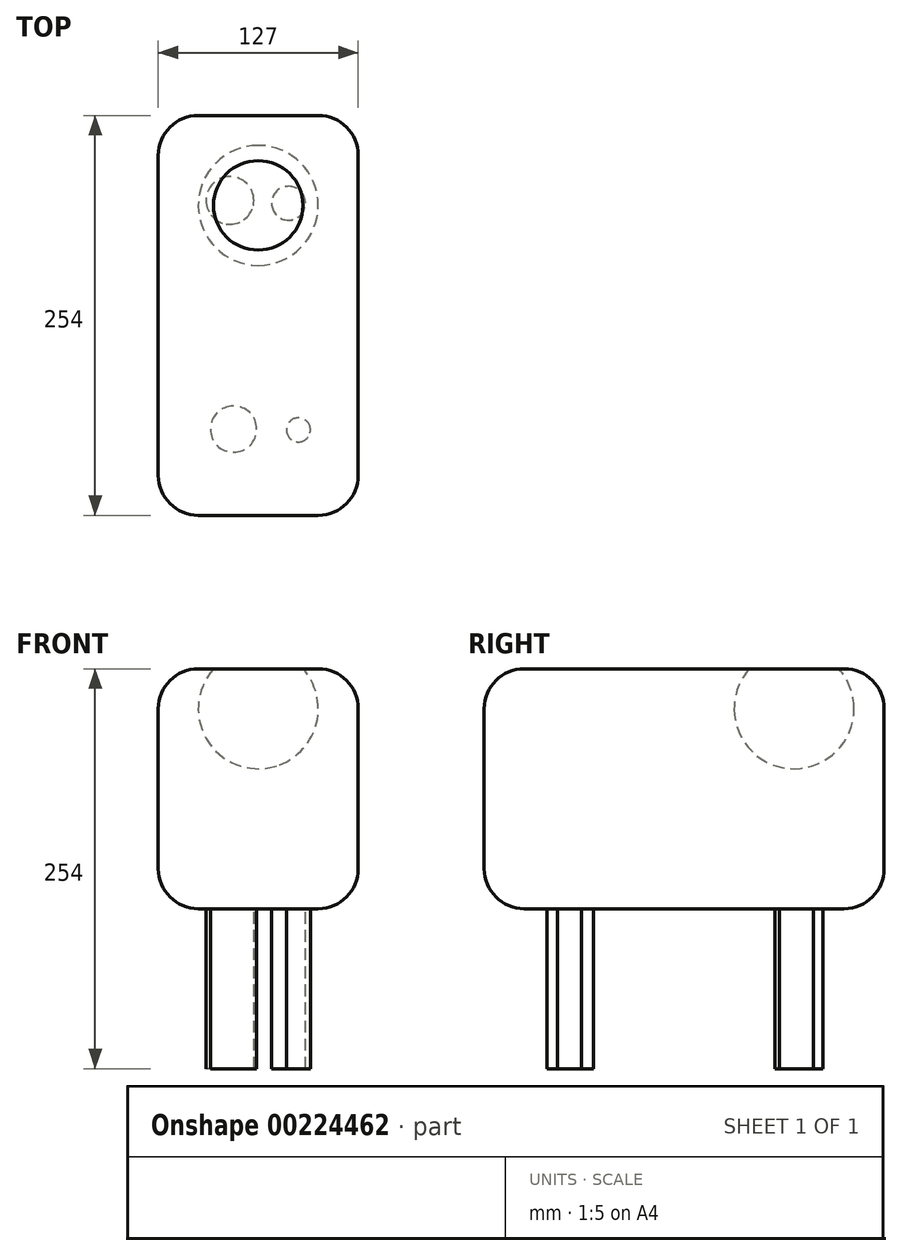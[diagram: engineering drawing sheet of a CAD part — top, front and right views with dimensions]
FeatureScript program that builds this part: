
annotation { "Feature Type Name" : "Feature", "Feature Type Description" : "" }
export const myFeature = defineFeature(function(context is Context, id is Id, definition is map)
    precondition{}
    {
        {
            var Q0;
            Q0=qCreatedBy(makeId("Right.planeOp"),FACE);
            var sketch = newSketch(context, id + "F0", { "sketchPlane" : qUnion([Q0])});
            skLineSegment(sketch, "E0.bottom", {"start": v(0, 0) * mm, "end": v(254, 0) * mm});
            skLineSegment(sketch, "E0.top", {"start": v(0, 152.4) * mm, "end": v(254, 152.4) * mm});
            skLineSegment(sketch, "E0.left", {"start": v(0, 0) * mm, "end": v(0, 152.4) * mm});
            skLineSegment(sketch, "E0.right", {"start": v(254, 0) * mm, "end": v(254, 152.4) * mm});
            skSolve(sketch);
        }
        {
            var Q0;
            Q0 = qSketchRegion(id + "F0", true);
            extrude(context, id + "F1", {"entities" : qUnion([Q0]), "depth" : 127 * mm});
        }
        {
            var Q0;
            Q0=makeQuery(id+"F1.opExtrude","SWEPT_FACE",FACE,{"disambiguationData":[OSD([sQuery(id+"F0.wireOp",EDGE,"E0.top")])]});
            var Q1;
            Q1=makeQuery(id+"F1.opExtrude","SWEPT_FACE",FACE,{"disambiguationData":[OSD([sQuery(id+"F0.wireOp",EDGE,"E0.right")])]});
            var Q2;
            Q2=makeQuery(id+"F1.opExtrude","CAP_FACE",FACE,{"disambiguationData":[OSD([sQuery(id+"F0.wireOp",EDGE,"E0.bottom"),sQuery(id+"F0.wireOp",EDGE,"E0.top"),sQuery(id+"F0.wireOp",EDGE,"E0.left"),sQuery(id+"F0.wireOp",EDGE,"E0.right")])],"isStart":false});
            var Q3;
            Q3=makeQuery(id+"F1.opExtrude","CAP_FACE",FACE,{"disambiguationData":[OSD([sQuery(id+"F0.wireOp",EDGE,"E0.bottom"),sQuery(id+"F0.wireOp",EDGE,"E0.top"),sQuery(id+"F0.wireOp",EDGE,"E0.left"),sQuery(id+"F0.wireOp",EDGE,"E0.right")])],"isStart":true});
            var Q4;
            Q4=makeQuery(id+"F1.opExtrude","SWEPT_FACE",FACE,{"disambiguationData":[OSD([sQuery(id+"F0.wireOp",EDGE,"E0.bottom")])]});
            fillet(context, id + "F2", {"entities" : qUnion([Q0, Q1, Q2, Q3, Q4]), "radius" : 25.4 * mm, "tangentPropagation" : true, "allowEdgeOverflow" : false});
        }
        {
            var Q0;
            Q0=makeQuery(id+"F1.opExtrude","SWEPT_FACE",FACE,{"disambiguationData":[OSD([sQuery(id+"F0.wireOp",EDGE,"E0.top")])]});
            cPlane(context, id + "F3", {"entities" : qUnion([Q0]), "cplaneType" : CPlaneType.OFFSET, "offset" : 25.4 * mm, "oppositeDirection" : true, "width" : 152.4 * mm, "height" : 152.4 * mm});
        }
        {
            var Q0;
            Q0=qCreatedBy(id+"F3.planeOp",FACE);
            var sketch = newSketch(context, id + "F4", { "sketchPlane" : qUnion([Q0])});
            skArc(sketch, "E1", {"start": v(63.5, 234.95) * mm, "mid": v(25.4, 196.85) * mm, "end": v(63.5, 158.75) * mm});
            skLineSegment(sketch, "E2", {"start": v(63.5, 234.95) * mm, "end": v(63.5, 158.75) * mm});
            skSolve(sketch);
        }
        {
            var Q0;
            Q0 = qSketchRegion(id + "F4", true);
            var Q1;
            Q1=sQuery(id+"F4.wireOp",EDGE,"E2");
            revolve(context, id + "F5", {"operationType" : NewBodyOperationType.REMOVE, "entities" : qUnion([Q0]), "axis" : qUnion([Q1]), "revolveType" : RevolveType.FULL, "oppositeDirection" : true});
        }
        {
            var Q0;
            Q0=makeQuery(id+"F1.opExtrude","SWEPT_FACE",FACE,{"disambiguationData":[OSD([sQuery(id+"F0.wireOp",EDGE,"E0.bottom")])]});
            var sketch = newSketch(context, id + "F6", { "sketchPlane" : qUnion([Q0])});
            skCircle(sketch, "E3", {"center": v(47.78, -54.72) * mm, "radius": 14.69 * mm});
            skCircle(sketch, "E4", {"center": v(89.03, -54.27) * mm, "radius": 7.66 * mm});
            skCircle(sketch, "E5", {"center": v(45.54, -199.99) * mm, "radius": 15.17 * mm});
            skCircle(sketch, "E6", {"center": v(82.76, -198.2) * mm, "radius": 10.76 * mm});
            skSolve(sketch);
        }
        {
            var Q0;
            Q0=makeQuery(id+"F6.imprint","IMPRINT",FACE,{"disambiguationData":[TD([[makeQuery(id+"F6.imprint","IMPRINT",EDGE,{"derivedFrom":sQuery(id+"F6.wireOp",EDGE,"E3")}),1.0]])]});
            var Q1;
            Q1=makeQuery(id+"F6.imprint","IMPRINT",FACE,{"disambiguationData":[TD([[makeQuery(id+"F6.imprint","IMPRINT",EDGE,{"derivedFrom":sQuery(id+"F6.wireOp",EDGE,"E4")}),1.0]])]});
            var Q2;
            Q2=makeQuery(id+"F6.imprint","IMPRINT",FACE,{"disambiguationData":[TD([[makeQuery(id+"F6.imprint","IMPRINT",EDGE,{"derivedFrom":sQuery(id+"F6.wireOp",EDGE,"E5")}),1.0]])]});
            var Q3;
            Q3=makeQuery(id+"F6.imprint","IMPRINT",FACE,{"disambiguationData":[TD([[makeQuery(id+"F6.imprint","IMPRINT",EDGE,{"derivedFrom":sQuery(id+"F6.wireOp",EDGE,"E6")}),1.0]])]});
            extrude(context, id + "F7", {"entities" : qUnion([Q0, Q1, Q2, Q3]), "operationType" : NewBodyOperationType.ADD, "depth" : 101.6 * mm});
        }
    });
